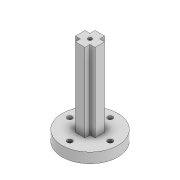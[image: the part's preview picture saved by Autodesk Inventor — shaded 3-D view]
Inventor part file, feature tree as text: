
AUTODESK INVENTOR PART (.ipt)
format: ipt  version: 2022 (Build 260153000, 153)  size: 144,384 bytes
history: native  units: mm
features: extrude x6, sketch x6, pattern_circular x1
ambient origin geometry x8: Origin, YZ Plane, XZ Plane, XY Plane, X Axis, Y Axis, Z Axis, Center Point
bodies: Solid1 (feature_tree)
feature tree (13):
  extrude  "Extrusion1"  Depth=4.0mm TaperAngle=0.0deg
  extrude  "Extrusion2"  Depth=8.0mm
  pattern_circular  "Circular Pattern1"  Count=4 Angle=360.0deg
  extrude  "Extrusion3"  Depth=7.8mm
  extrude  "Extrusion4"  Depth=2.0mm
  extrude  "Extrusion5"  Depth=3.0mm
  extrude  "Extrusion6"  Depth=8.0mm TaperAngle=0.0deg
  sketch  "Sketch1"  dims[d0=22.0mm d1=4.0mm d2=0.0mm]
  sketch  "Sketch2"  dims[d3=2.0mm d4=8.0mm]
  sketch  "Sketch3"  dims[d5=10.0mm d6=0.0mm d7=40.0mm d8=360.0deg]
  sketch  "Sketch4"  dims[d10=7.8mm d11=7.8mm]
  sketch  "Sketch5"  dims[d12=31.0mm d13=0.0mm d14=2.0mm]
  sketch  "Sketch6"  dims[d15=2.0mm d16=1.5mm d17=8.0mm d18=0.0mm d19=10.0mm d20=2.2mm d21=0.0mm d22=5.0mm d23=3.0mm d24=0.0mm]
